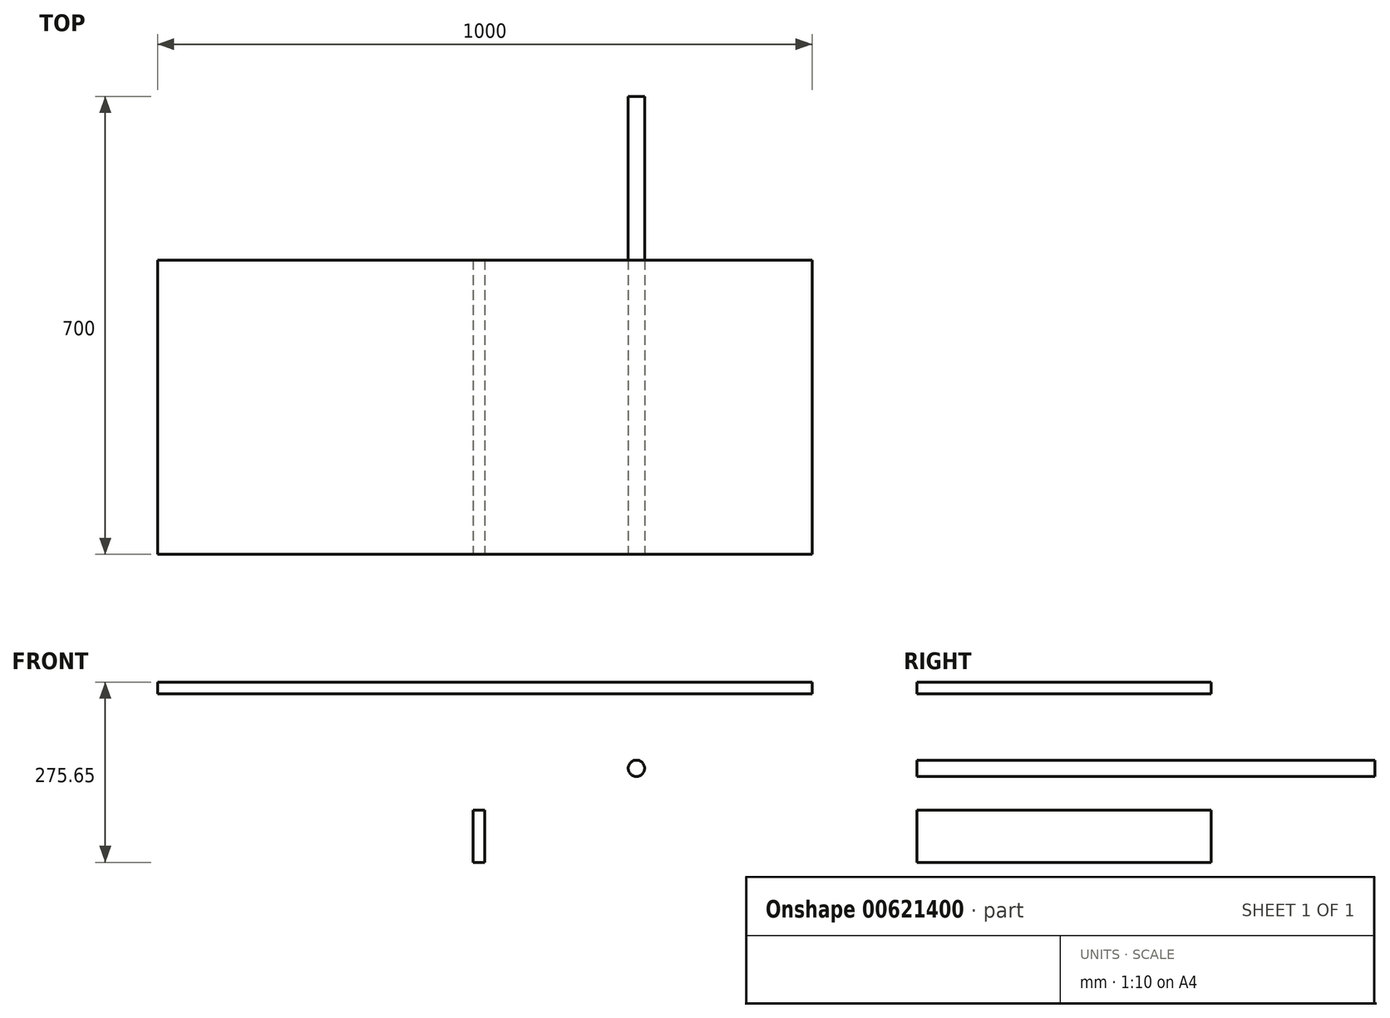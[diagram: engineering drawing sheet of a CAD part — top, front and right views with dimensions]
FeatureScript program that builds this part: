
annotation { "Feature Type Name" : "Feature", "Feature Type Description" : "" }
export const myFeature = defineFeature(function(context is Context, id is Id, definition is map)
    precondition{}
    {
        {
            var Q0;
            Q0=qCreatedBy(makeId("Front.planeOp"),FACE);
            var sketch = newSketch(context, id + "F0", { "sketchPlane" : qUnion([Q0])});
            skLineSegment(sketch, "E0.bottom", {"start": v(500, 9) * mm, "end": v(-500, 9) * mm});
            skLineSegment(sketch, "E0.top", {"start": v(500, -9) * mm, "end": v(-500, -9) * mm});
            skLineSegment(sketch, "E0.left", {"start": v(500, 9) * mm, "end": v(500, -9) * mm});
            skLineSegment(sketch, "E0.right", {"start": v(-500, 9) * mm, "end": v(-500, -9) * mm});
            skPoint(sketch, "E0.middle", {"position": v(0, 0) * mm});
            skSolve(sketch);
        }
        {
            var Q0;
            Q0 = qSketchRegion(id + "F0", true);
            extrude(context, id + "F1", {"entities" : qUnion([Q0]), "oppositeDirection" : true, "depth" : 450 * mm, "offsetDistance" : 25 * mm});
        }
        {
            var Q0;
            Q0=qCreatedBy(makeId("Front.planeOp"),FACE);
            var sketch = newSketch(context, id + "F2", { "sketchPlane" : qUnion([Q0])});
            skLineSegment(sketch, "E1.bottom", {"start": v(-18, -186.65) * mm, "end": v(0, -186.65) * mm});
            skLineSegment(sketch, "E1.top", {"start": v(-18, -266.65) * mm, "end": v(0, -266.65) * mm});
            skLineSegment(sketch, "E1.left", {"start": v(-18, -186.65) * mm, "end": v(-18, -266.65) * mm});
            skLineSegment(sketch, "E1.right", {"start": v(0, -186.65) * mm, "end": v(0, -266.65) * mm});
            skSolve(sketch);
        }
        {
            var Q0;
            Q0 = qSketchRegion(id + "F2", true);
            extrude(context, id + "F3", {"entities" : qUnion([Q0]), "oppositeDirection" : true, "depth" : 450 * mm, "offsetDistance" : 25 * mm});
        }
        {
            var Q0;
            Q0=qCreatedBy(makeId("Front.planeOp"),FACE);
            var sketch = newSketch(context, id + "F4", { "sketchPlane" : qUnion([Q0])});
            skCircle(sketch, "E2", {"center": v(231.65, -122.93) * mm, "radius": 12.5 * mm});
            skSolve(sketch);
        }
        {
            var Q0;
            Q0 = qSketchRegion(id + "F4", true);
            extrude(context, id + "F5", {"entities" : qUnion([Q0]), "oppositeDirection" : true, "depth" : 700 * mm, "offsetDistance" : 25 * mm});
        }
    });
